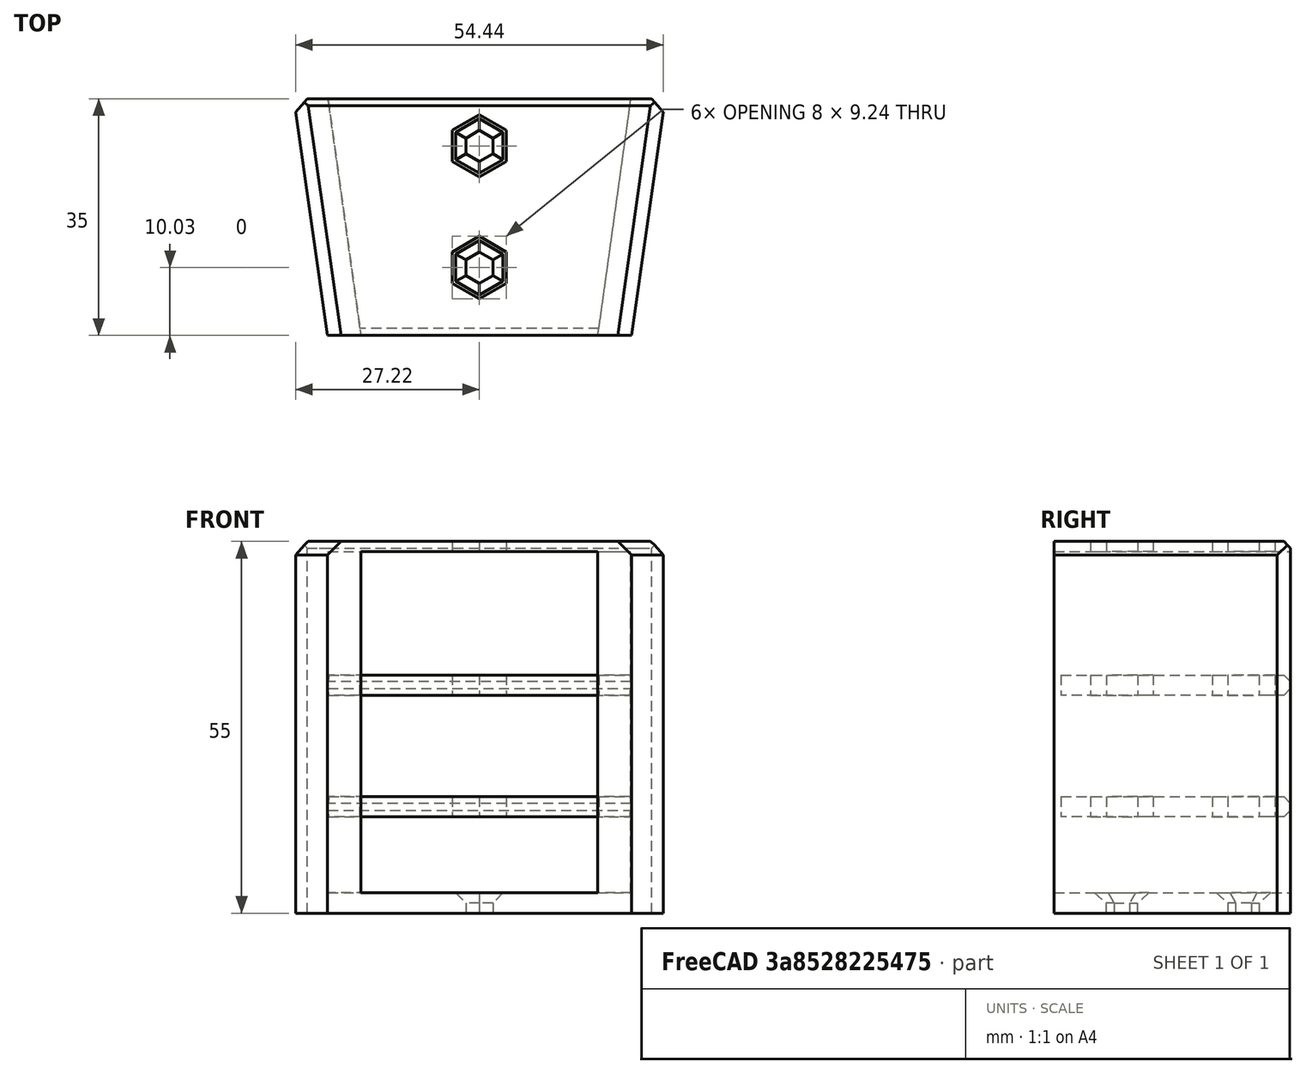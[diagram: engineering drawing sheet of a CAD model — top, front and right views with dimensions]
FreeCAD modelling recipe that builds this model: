
FCSTD DOCUMENT  (FreeCAD 0.19R)
Label: PlierHolders
License: All rights reserved
LicenseURL: http://en.wikipedia.org/wiki/All_rights_reserved
objects: Sketcher::SketchObject×7, PartDesign::Chamfer×4, PartDesign::Pad×3, PartDesign::Pocket×3, PartDesign::Body×1, Mesh::Feature×1
note: 28 computed .brp shape members not serialized (recipe doc carries the construction recipe); baked Part::Feature solids carry a one-line shape summary decoded from their .brp

FEATURE [Sketcher::SketchObject] Sketch
  FullyConstrained = true
  MapMode = 5
  Support = -> [XY_Plane]
  sketch-geometry (4):
    g0: LineSegment StartX=-27.5 StartY=35 StartZ=0 EndX=-22.5 EndY=0 EndZ=0
    g1: LineSegment StartX=-22.5 StartY=0 StartZ=0 EndX=22.5 EndY=0 EndZ=0
    g2: LineSegment StartX=22.5 StartY=0 StartZ=0 EndX=27.5 EndY=35 EndZ=0
    g3: LineSegment StartX=27.5 StartY=35 StartZ=0 EndX=-27.5 EndY=35 EndZ=0
  constraints (10):
    c: PointOnObject(g0,g-1)
    c: Coincident(g0,g1)
    c: Coincident(g1,g2)
    c: Coincident(g2,g3)
    c: Coincident(g3,g0)
    c: Distance(g3) = 55
    c: Distance(g1) = 45
    c: Symmetric(g1,g0,g-2)
    c: Symmetric(g2,g0,g-2)
    c: DistanceY(g2) = 35
FEATURE [PartDesign::Pad] Pad
  Direction = (1,1,1)
  Length = 55
  Length2 = 100
  Profile = -> Sketch
  Type = 0
FEATURE [Sketcher::SketchObject] Sketch001
  FullyConstrained = true
  MapMode = 5
  Placement = pos=(0,0,55) rot=(0,0,1;0rad)
  Support = -> [Pad]
FEATURE [Sketcher::SketchObject] Sketch002
  FullyConstrained = false
  MapMode = 5
  Placement = pos=(0,0,55) rot=(0,0,1;0rad)
  Support = -> [Pad]
  sketch-geometry (4):
    g0: LineSegment StartX=-22.5 StartY=35.6173 StartZ=0 EndX=-17.5 EndY=-0.246526 EndZ=0
    g1: LineSegment StartX=-17.5 StartY=-0.246526 StartZ=0 EndX=17.5 EndY=-0.246526 EndZ=0
    g2: LineSegment StartX=17.5 StartY=-0.246526 StartZ=0 EndX=22.5 EndY=35.6173 EndZ=0
    g3: LineSegment StartX=22.5 StartY=35.6173 StartZ=0 EndX=-22.5 EndY=35.6173 EndZ=0
  constraints (8):
    c: Coincident(g0,g1)
    c: Coincident(g1,g2)
    c: Coincident(g2,g3)
    c: Coincident(g3,g0)
    c: Distance(g3) = 45
    c: Distance(g1) = 35
    c: Symmetric(g1,g0,g-2)
    c: Symmetric(g2,g0,g-2)
FEATURE [PartDesign::Pocket] Pocket
  BaseFeature = -> Pad
  Length = 52
  Length2 = 100
  Profile = -> Sketch002
  Type = 0
FEATURE [Sketcher::SketchObject] Sketch003
  FullyConstrained = false
  MapMode = 5
  Placement = pos=(0,0,55) rot=(0,0,1;0rad)
  Support = -> [Pocket]
  sketch-geometry (4):
    g0: LineSegment StartX=-23.6773 StartY=35 StartZ=0 EndX=23.6798 EndY=35 EndZ=0
    g1: LineSegment StartX=23.6798 StartY=35 StartZ=0 EndX=18.6121 EndY=0 EndZ=0
    g2: LineSegment StartX=18.6121 StartY=0 StartZ=0 EndX=-18.2612 EndY=0 EndZ=0
    g3: LineSegment StartX=-18.2612 StartY=0 StartZ=0 EndX=-23.6773 EndY=35 EndZ=0
  constraints (8):
    c: Horizontal(g0)
    c: Coincident(g0,g1)
    c: PointOnObject(g1,g-1)
    c: Coincident(g1,g2)
    c: PointOnObject(g2,g-1)
    c: Coincident(g2,g3)
    c: Coincident(g3,g0)
    c: DistanceY(g0) = 35
FEATURE [PartDesign::Pad] Pad001
  BaseFeature = -> Pocket
  Direction = (1,1,1)
  Length = 1.5
  Length2 = 100
  Profile = -> Sketch003
  Reversed = true
  Type = 0
FEATURE [Sketcher::SketchObject] Sketch004
  FullyConstrained = false
  MapMode = 5
  Placement = pos=(0,0,55) rot=(0,0,1;0rad)
  Support = -> [Pad001]
  sketch-geometry (14):
    g0: LineSegment StartX=2 StartY=29.184 StartZ=0 EndX=0 EndY=30.3387 EndZ=0
    g1: LineSegment StartX=0 StartY=30.3387 StartZ=0 EndX=-2 EndY=29.184 EndZ=0
    g2: LineSegment StartX=-2 StartY=29.184 StartZ=0 EndX=-2 EndY=26.8746 EndZ=0
    g3: LineSegment StartX=-2 StartY=26.8746 StartZ=0 EndX=0 EndY=25.7199 EndZ=0
    g4: LineSegment StartX=0 StartY=25.7199 StartZ=0 EndX=2 EndY=26.8746 EndZ=0
    g5: LineSegment StartX=2 StartY=26.8746 StartZ=0 EndX=2 EndY=29.184 EndZ=0
    g6: Circle CenterX=0 CenterY=28.0293 CenterZ=0 NormalX=0 NormalY=0 NormalZ=1 AngleXU=0 Radius=2.3094
    g7: LineSegment StartX=2 StartY=8.84962 StartZ=0 EndX=2 EndY=11.159 EndZ=0
    g8: LineSegment StartX=2 StartY=11.159 StartZ=0 EndX=0 EndY=12.3137 EndZ=0
    g9: LineSegment StartX=0 StartY=12.3137 StartZ=0 EndX=-2 EndY=11.159 EndZ=0
    g10: LineSegment StartX=-2 StartY=11.159 StartZ=0 EndX=-2 EndY=8.84962 EndZ=0
    g11: LineSegment StartX=-2 StartY=8.84962 StartZ=0 EndX=0 EndY=7.69492 EndZ=0
    g12: LineSegment StartX=0 StartY=7.69492 StartZ=0 EndX=2 EndY=8.84962 EndZ=0
    g13: Circle CenterX=0 CenterY=10.0043 CenterZ=0 NormalX=0 NormalY=0 NormalZ=1 AngleXU=0 Radius=2.3094
  constraints (32):
    c: Coincident(g0,g1)
    c: Coincident(g1,g2)
    c: Coincident(g2,g3)
    c: Coincident(g3,g4)
    c: Coincident(g4,g5)
    c: Coincident(g5,g0)
    c: Equal(g0, g1-g5) x5
    c: PointOnObject(g0,g6)
    c: PointOnObject(g1,g6)
    c: PointOnObject(g2,g6)
    c: PointOnObject(g3,g6)
    c: PointOnObject(g4,g6)
    c: PointOnObject(g5,g6)
    c: PointOnObject(g6,g-2)
    c: Coincident(g7,g8)
    c: Coincident(g8,g9)
    c: Coincident(g9,g10)
    c: Coincident(g10,g11)
    c: Coincident(g11,g12)
    c: Coincident(g12,g7)
    c: Equal(g7, g8-g12) x5
    c: PointOnObject(g7,g13)
    c: PointOnObject(g8,g13)
    c: PointOnObject(g9,g13)
    c: PointOnObject(g10,g13)
    c: PointOnObject(g11,g13)
    c: PointOnObject(g12,g13)
    c: PointOnObject(g13,g-2)
    c: Distance(g8,g10) = 4
    c: Distance(g1,g3) = 4
    c: Vertical(g2)
    c: Vertical(g10)
FEATURE [Sketcher::SketchObject] Sketch005
  FullyConstrained = false
  MapMode = 5
  Placement = pos=(0,0,55) rot=(0,0,1;0rad)
  sketch-geometry (14):
    g0: LineSegment StartX=4 StartY=25.7311 StartZ=0 EndX=4 EndY=30.3499 EndZ=0
    g1: LineSegment StartX=4 StartY=30.3499 StartZ=0 EndX=0 EndY=32.6593 EndZ=0
    g2: LineSegment StartX=0 StartY=32.6593 StartZ=0 EndX=-4 EndY=30.3499 EndZ=0
    g3: LineSegment StartX=-4 StartY=30.3499 StartZ=0 EndX=-4 EndY=25.7311 EndZ=0
    g4: LineSegment StartX=-4 StartY=25.7311 StartZ=0 EndX=0 EndY=23.4217 EndZ=0
    g5: LineSegment StartX=0 StartY=23.4217 StartZ=0 EndX=4 EndY=25.7311 EndZ=0
    g6: Circle CenterX=0 CenterY=28.0405 CenterZ=0 NormalX=0 NormalY=0 NormalZ=1 AngleXU=0 Radius=4.6188
    g7: LineSegment StartX=4 StartY=7.72029 StartZ=0 EndX=4 EndY=12.3391 EndZ=0
    g8: LineSegment StartX=4 StartY=12.3391 StartZ=0 EndX=0 EndY=14.6485 EndZ=0
    g9: LineSegment StartX=0 StartY=14.6485 StartZ=0 EndX=-4 EndY=12.3391 EndZ=0
    g10: LineSegment StartX=-4 StartY=12.3391 StartZ=0 EndX=-4 EndY=7.72029 EndZ=0
    g11: LineSegment StartX=-4 StartY=7.72029 StartZ=0 EndX=0 EndY=5.41089 EndZ=0
    g12: LineSegment StartX=0 StartY=5.41089 StartZ=0 EndX=4 EndY=7.72029 EndZ=0
    g13: Circle CenterX=0 CenterY=10.0297 CenterZ=0 NormalX=0 NormalY=0 NormalZ=1 AngleXU=0 Radius=4.6188
  constraints (32):
    c: Coincident(g0,g1)
    c: Coincident(g1,g2)
    c: Coincident(g2,g3)
    c: Coincident(g3,g4)
    c: Coincident(g4,g5)
    c: Coincident(g5,g0)
    c: Equal(g0, g1-g5) x5
    c: PointOnObject(g0,g6)
    c: PointOnObject(g1,g6)
    c: PointOnObject(g2,g6)
    c: PointOnObject(g3,g6)
    c: PointOnObject(g4,g6)
    c: PointOnObject(g5,g6)
    c: PointOnObject(g6,g-2)
    c: Coincident(g7,g8)
    c: Coincident(g8,g9)
    c: Coincident(g9,g10)
    c: Coincident(g10,g11)
    c: Coincident(g11,g12)
    c: Coincident(g12,g7)
    c: Equal(g7, g8-g12) x5
    c: PointOnObject(g7,g13)
    c: PointOnObject(g8,g13)
    c: PointOnObject(g9,g13)
    c: PointOnObject(g10,g13)
    c: PointOnObject(g11,g13)
    c: PointOnObject(g12,g13)
    c: PointOnObject(g13,g-2)
    c: Vertical(g10)
    c: Vertical(g3)
    c: Distance(g0,g2) = 8
    c: Distance(g7,g9) = 8
FEATURE [Sketcher::SketchObject] Sketch007
  FullyConstrained = false
  MapMode = 5
  Placement = pos=(0,35,0) rot=(0,0.707107,0.707107;3.14159rad)
  Support = -> [Pad001]
  sketch-geometry (8):
    g0: LineSegment StartX=-22.5 StartY=35.2425 StartZ=0 EndX=22.5 EndY=35.2425 EndZ=0
    g1: LineSegment StartX=22.5 StartY=35.2425 StartZ=0 EndX=22.5 EndY=32.2425 EndZ=0
    g2: LineSegment StartX=22.5 StartY=32.2425 StartZ=0 EndX=-22.5 EndY=32.2425 EndZ=0
    g3: LineSegment StartX=-22.5 StartY=32.2425 StartZ=0 EndX=-22.5 EndY=35.2425 EndZ=0
    g4: LineSegment StartX=-22.5 StartY=17.2425 StartZ=0 EndX=22.5 EndY=17.2425 EndZ=0
    g5: LineSegment StartX=22.5 StartY=17.2425 StartZ=0 EndX=22.5 EndY=14.2425 EndZ=0
    g6: LineSegment StartX=22.5 StartY=14.2425 StartZ=0 EndX=-22.5 EndY=14.2425 EndZ=0
    g7: LineSegment StartX=-22.5 StartY=14.2425 StartZ=0 EndX=-22.5 EndY=17.2425 EndZ=0
  constraints (21):
    c: Coincident(g0,g1)
    c: Coincident(g1,g2)
    c: Coincident(g2,g3)
    c: Coincident(g3,g0)
    c: Horizontal(g2)
    c: Vertical(g1)
    c: Vertical(g3)
    c: Coincident(g4,g5)
    c: Coincident(g5,g6)
    c: Coincident(g6,g7)
    c: Coincident(g7,g4)
    c: Horizontal(g6)
    c: Vertical(g5)
    c: Vertical(g7)
    c: Distance(g5) = 3
    c: Distance(g1) = 3
    c: Distance(g4,g2) = 15
    c: Distance(g0) = 45
    c: Symmetric(g0,g0,g-2)
    c: Equal(g4,g0)
    c: Symmetric(g4,g4,g-2)
FEATURE [PartDesign::Pad] Pad002
  BaseFeature = -> Pad001
  Direction = (1,1,1)
  Length = 34
  Length2 = 100
  Profile = -> Sketch007
  Reversed = true
  Type = 0
FEATURE [PartDesign::Pocket] Pocket001
  BaseFeature = -> Pad002
  Length = 5
  Length2 = 100
  Profile = -> Sketch004
  Type = 1
FEATURE [PartDesign::Pocket] Pocket002
  BaseFeature = -> Pocket001
  Length = 43
  Length2 = 100
  Profile = -> Sketch005
  Type = 0
FEATURE [PartDesign::Chamfer] Chamfer
  Angle = 45
  Base = -> Pocket002 [Edge80,Edge79,Edge78,Edge77,Edge76,Edge81,Edge70,Edge71,Edge72,Edge73,Edge74,Edge75]
  BaseFeature = -> Pocket002
  ChamferType = 0
  FlipDirection = false
  Size = 1.5
  Size2 = 1
  SupportTransform = false
FEATURE [PartDesign::Chamfer] Chamfer001
  Angle = 45
  Base = -> Chamfer [Edge123,Edge113,Edge55,Edge30]
  BaseFeature = -> Chamfer
  ChamferType = 0
  FlipDirection = false
  Size = 2
  Size2 = 1
  SupportTransform = false
FEATURE [PartDesign::Chamfer] Chamfer002
  Angle = 45
  Base = -> Chamfer001 [Face43,Face44]
  BaseFeature = -> Chamfer001
  ChamferType = 0
  FlipDirection = false
  Size = 1
  Size2 = 1
  SupportTransform = false
FEATURE [PartDesign::Chamfer] Chamfer003
  Angle = 45
  Base = -> Chamfer002 [Edge209]
  BaseFeature = -> Chamfer002
  ChamferType = 0
  FlipDirection = false
  Size = 1
  Size2 = 1
  SupportTransform = false
FEATURE [PartDesign::Body] Body
  Group = -> [Sketch,Pad,Sketch001,Sketch002,Pocket,Sketch003,Pad001,Sketch004,Sketch005,Sketch007,Pad002,Pocket001,Pocket002,Chamfer,Chamfer001,Chamfer002,Chamfer003]
  Origin = -> Origin
  Tip = -> Chamfer003
FEATURE [Mesh::Feature] Mesh  label="Chamfer003 (Meshed)"
